# Revit family: Caroma Leda Care Invisi Wall Faced Suite
name_source: partatom
category: Plumbing Fixtures
revit_build: Autodesk Revit LT 2014 (Build: 20130308_1515(x64)
units: mm (PartAtom-declared; Revit-internal decimal feet)

## types (1)
- Standard
    Assembly Code = D2010110
    Backrest = Yes
    CW Connection = Yes
    CWFU = 1.18
    Default Elevation = 0 mm  [stored 0 ft]
    Description = Caroma Leda Care Wall Faced Invisi II Suite
    HW Connection = No
    Hardware = Metal-Stainless Steel-Brushed
    Height_ANZRS = 966 mm
    Keynote = WC
    Length_ANZRS = 800 mm  [stored 2.62467 ft]
    Manufacturer = GWA Bathrooms & Kitchens
    Material_ANZRS = Porcelain-White-Caroma
    Model = 719105BW
    ModifiedIssue_ANZRS = 20140917.01 $
    No Backrest = No
    Seat = Porcelain-Sorrento Blue-Caroma
    Type Comments = White Only, S Trap Only, Buttons and Panels sold separately
    URL = http://www.caroma.com.au
    Vent Connection = No
    WELSRating_ANZRS = WELS 4 Star rated, 4.5/3L
    WFU = 1.18
    Waste Connection = Yes
    WasteOutlet_ANZRS = 0
    Width_ANZRS = 350 mm  [stored 1.14829 ft]

note: [stored X ft] marks values corroborated as IEEE doubles in the binary element streams (Revit-internal decimal feet)

## geometry (parser evidence)
native form markers: Blend x16, Sweep x3
no freeform markers — native parametric forms only
